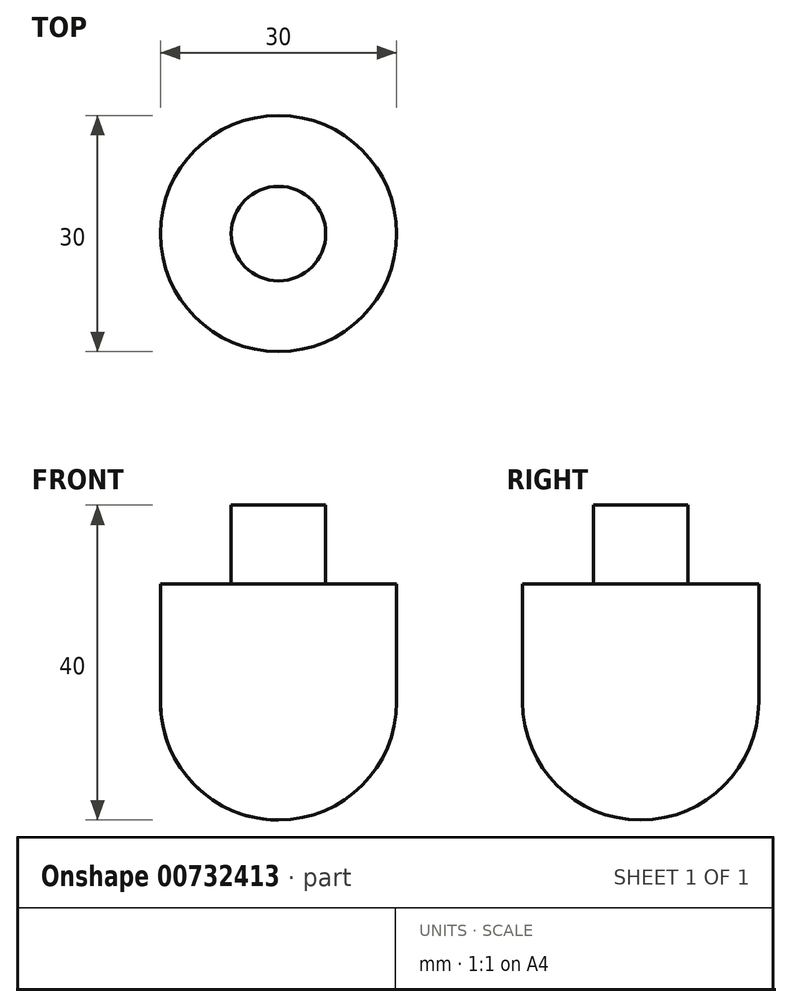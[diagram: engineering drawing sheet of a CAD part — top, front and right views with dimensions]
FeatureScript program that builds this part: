
annotation { "Feature Type Name" : "Feature", "Feature Type Description" : "" }
export const myFeature = defineFeature(function(context is Context, id is Id, definition is map)
    precondition{}
    {
        {
            var Q0;
            Q0=qCreatedBy(makeId("Front.planeOp"),FACE);
            var sketch = newSketch(context, id + "F0", { "sketchPlane" : qUnion([Q0])});
            skLineSegment(sketch, "E0", {"start": v(0, 25) * mm, "end": v(-6, 25) * mm});
            skLineSegment(sketch, "E1", {"start": v(-6, 25) * mm, "end": v(-6, 15) * mm});
            skLineSegment(sketch, "E2", {"start": v(-6, 15) * mm, "end": v(-15, 15) * mm});
            skLineSegment(sketch, "E3", {"start": v(-15, 15) * mm, "end": v(-15, 0) * mm});
            skLineSegment(sketch, "E4", {"start": v(0, -15) * mm, "end": v(0, 25) * mm});
            skArc(sketch, "E5", {"start": v(-15, 0) * mm, "mid": v(-10.6, -10.6) * mm, "end": v(0, -15) * mm});
            skSolve(sketch);
        }
        {
            var Q0;
            Q0=makeQuery(id+"F0.imprint","IMPRINT",FACE,{"disambiguationData":[TD([[makeQuery(id+"F0.imprint","IMPRINT",EDGE,{"derivedFrom":sQuery(id+"F0.wireOp",EDGE,"E0")}),1.0]])]});
            var Q1;
            Q1=sQuery(id+"F0.wireOp",EDGE,"E4");
            revolve(context, id + "F1", {"surfaceOperationType" : NewSurfaceOperationType.NEW, "entities" : qUnion([Q0]), "axis" : qUnion([Q1]), "revolveType" : RevolveType.FULL});
        }
    });
